# Revit family: SPP-4310-PD
name_source: partatom
category: Plumbing Fixtures
units: mm (PartAtom-declared; Revit-internal decimal feet)

## family parameters
Cut with Voids When Loaded = No
Host = Face
OmniClass Number = 23.65.55.00
OmniClass Title = Distribution of Supplied Liquids/Gases
Part Type = Normal
Room Calculation Point = No
Round Connector Dimension = Use Diameter
Shared = No

## types (6) — shared parameters
CW Connection = No
Gallons Per Minute = 2 GPM
HW Connection = No
Vent Connection = No
Waste Connection = No
zz Text 1 = None Selected
zz Text 2 = None Selected
zero-valued in all types: Default Elevation

## per-type parameters (varying)
| type | Product Material |
| 1.5 GPM, Polished Chrome | Chrome - Symmons - Polished |
| 1.5 GPM, Matte Black | Matte Black - Symmons |
| 1.5 GPM, Stainless Steel | Stainless - Symmons - Polished |
| 2.2 GPM, Matte Black | Matte Black - Symmons |
| 2.2 GPM, Polished Chrome | Chrome - Symmons - Polished |
| 2.2 GPM, Stainless Steel | Stainless - Symmons - Polished |

## geometry (parser evidence)
native form markers: Sweep x1
no freeform markers — native parametric forms only
